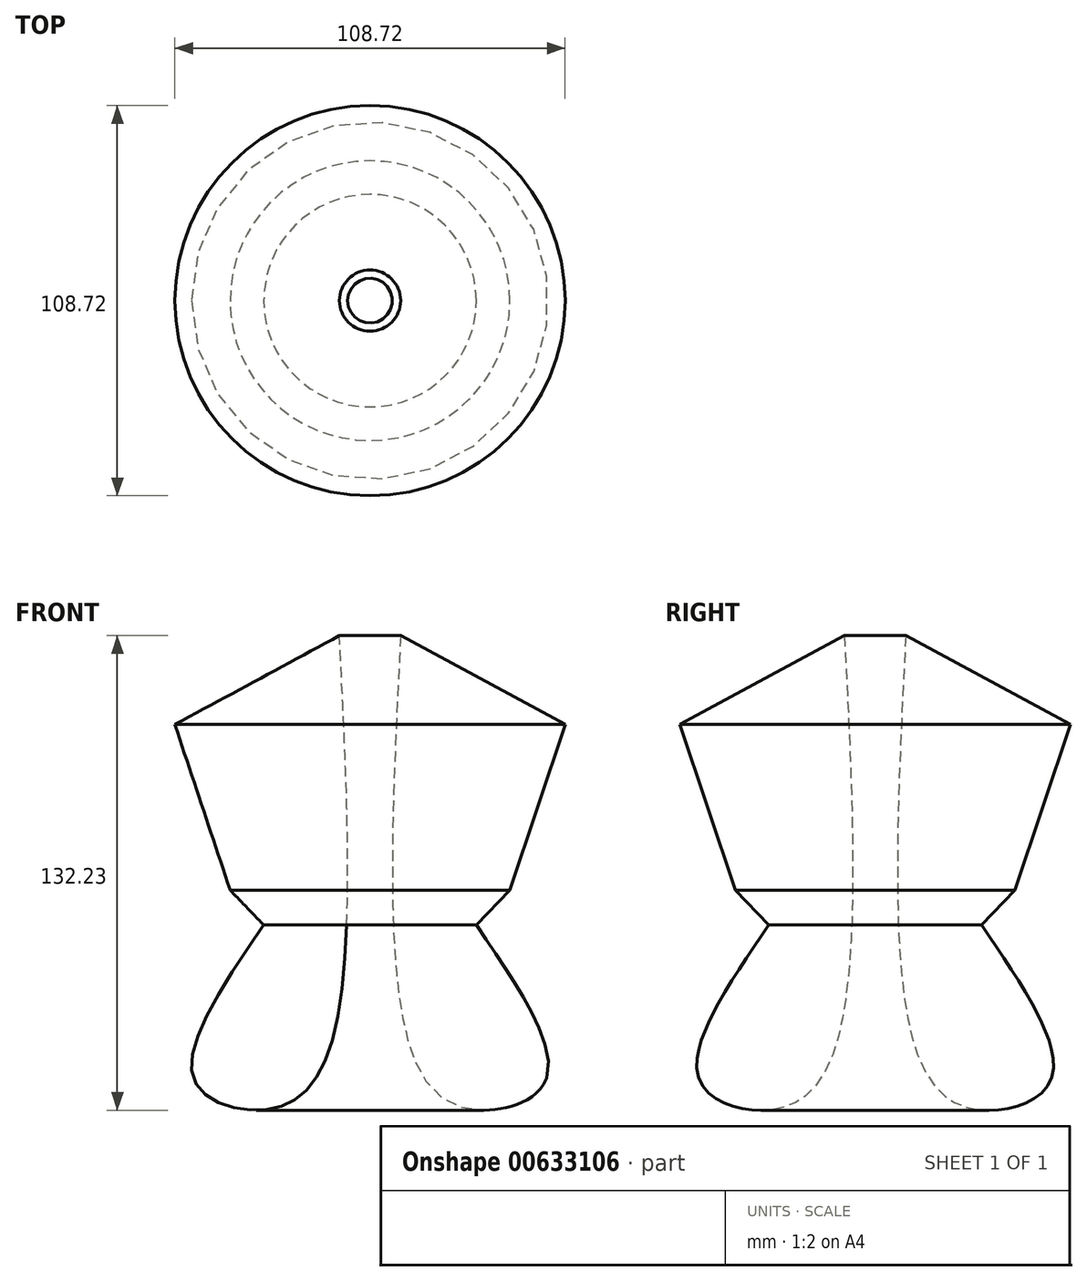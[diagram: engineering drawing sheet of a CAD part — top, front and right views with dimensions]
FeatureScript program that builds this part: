
annotation { "Feature Type Name" : "Feature", "Feature Type Description" : "" }
export const myFeature = defineFeature(function(context is Context, id is Id, definition is map)
    precondition{}
    {
        {
            var Q0;
            Q0=qCreatedBy(makeId("Top.planeOp"),FACE);
            var sketch = newSketch(context, id + "F0", { "sketchPlane" : qUnion([Q0])});
            skCircle(sketch, "E0", {"center": v(0, 0) * mm, "radius": 50 * mm});
            skSolve(sketch);
        }
        {
            var Q0;
            Q0=qCreatedBy(makeId("Front.planeOp"),FACE);
            var sketch = newSketch(context, id + "F1", { "sketchPlane" : qUnion([Q0])});
            skLineSegment(sketch, "E1", {"start": v(-8.53, 60.55) * mm, "end": v(-54.36, 35.8) * mm});
            skLineSegment(sketch, "E2", {"start": v(-54.36, 35.8) * mm, "end": v(-38.97, -10.37) * mm});
            skLineSegment(sketch, "E3", {"start": v(-38.97, -10.37) * mm, "end": v(-29.6, -20.07) * mm});
            skFitSpline(sketch, "E4", {"points": [v(-29.6, -20.07) * mm, v(-49.01, -63.23) * mm, v(-29.6, -71.6) * mm, v(-12.21, -57.2) * mm, v(-8.53, 60.55) * mm], "startDerivative": vector(-136.75, -200) * mm, "endDerivative": vector(-18.27, 360.22) * mm});
            skSolve(sketch);
        }
        {
            var Q0;
            Q0=makeQuery(id+"F1.imprint","IMPRINT",FACE,{"disambiguationData":[TD([[makeQuery(id+"F1.imprint","IMPRINT",EDGE,{"derivedFrom":sQuery(id+"F1.wireOp",EDGE,"E1")}),1.0]])]});
            var Q1;
            Q1=sQuery(id+"F0.wireOp",EDGE,"E0");
            revolve(context, id + "F2", {"entities" : qUnion([Q0]), "axis" : qUnion([Q1]), "revolveType" : RevolveType.FULL});
        }
    });
